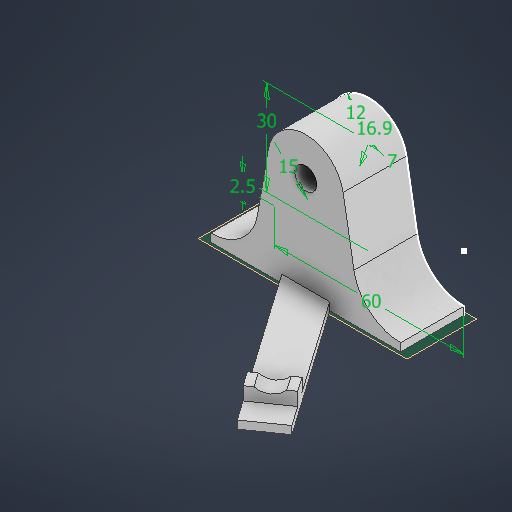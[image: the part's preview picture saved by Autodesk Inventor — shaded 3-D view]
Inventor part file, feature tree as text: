
AUTODESK INVENTOR PART (.ipt)
format: ipt  version: 2025.3 (Build 293356030, 356C)  size: 267,776 bytes
history: native  units: mm
features: extrude x7, sketch x3, plane x1, projected_geometry x1
ambient origin geometry x8: Origin, YZ Plane, XZ Plane, XY Plane, X Axis, Y Axis, Z Axis, Center Point
bodies: Solid1 (feature_tree)
feature tree (12):
  sketch  "Sketch1"  dims[d0=16.9mm d1=7.0mm d2=30.0mm d3=12.0mm d4=15.0mm d5=60.0mm d6=2.5mm d7=20.0mm d8=0.0mm]
  extrude  "Extrusion1"  Depth=20.0mm TaperAngle=0.0deg
  extrude  "Extrusion3"  TaperAngle=0.0deg  [1 undecoded]
  plane  "Work Plane1"
  sketch  "Sketch2"  dims[d11=20.0mm d12=0.0mm d13=0.0mm]
  extrude  "Extrusion6"  Depth=5.5mm
  sketch  "Sketch4"  dims[d14=6.108652mm d16=5.5mm d17=20.0mm d26=40.0mm d27=2.5mm d28=0.0mm d29=14.6mm d30=10.7mm d31=1.5mm d32=8.0mm d33=5.5mm d34=0.0mm d35=5.5mm d36=0.0mm d37=7.5mm d38=0.0mm d39=0.0mm d40=0.0mm]
  extrude  "Extrusion7"  Depth=20.0mm
  extrude  "Extrusion8"  Depth=7.5mm
  extrude  "Extrusion9"  Depth=2.5mm TaperAngle=0.0deg
  extrude  "Extrusion10"  Depth=7.5mm
  projected_geometry  "Projected Loop2"
note: 1 required parameter value undecoded (feature->parameter linkage not recoverable at this tier; creation-order binding heuristic only, values carry confidence <= 0.55)
